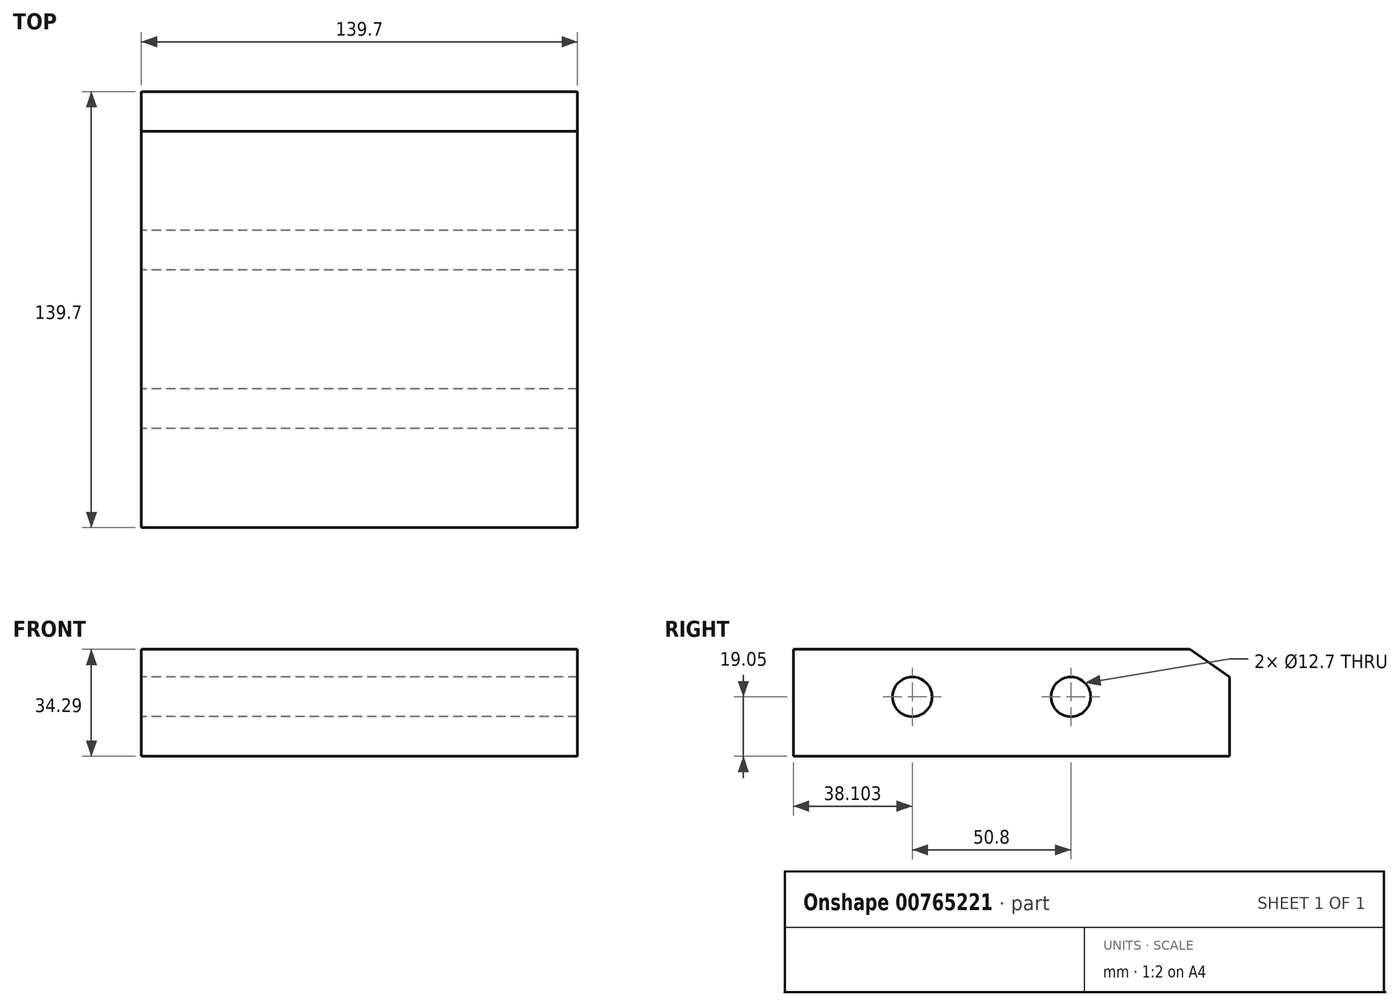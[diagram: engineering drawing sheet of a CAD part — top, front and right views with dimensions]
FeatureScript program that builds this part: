
annotation { "Feature Type Name" : "Feature", "Feature Type Description" : "" }
export const myFeature = defineFeature(function(context is Context, id is Id, definition is map)
    precondition{}
    {
        {
            var Q0;
            Q0=qCreatedBy(makeId("Right.planeOp"),FACE);
            var sketch = newSketch(context, id + "F0", { "sketchPlane" : qUnion([Q0])});
            skLineSegment(sketch, "E0", {"start": v(85.33, 0) * mm, "end": v(85.33, 15.24) * mm, "construction": true});
            skLineSegment(sketch, "E1", {"start": v(85.33, 15.24) * mm, "end": v(-41.67, 15.24) * mm});
            skLineSegment(sketch, "E2", {"start": v(-41.67, 15.24) * mm, "end": v(-41.67, -19.05) * mm});
            skLineSegment(sketch, "E3", {"start": v(-41.67, -19.05) * mm, "end": v(98.03, -19.05) * mm});
            skLineSegment(sketch, "E4", {"start": v(98.03, -19.05) * mm, "end": v(98.03, 6.35) * mm});
            skLineSegment(sketch, "E5", {"start": v(98.03, 6.35) * mm, "end": v(85.33, 15.24) * mm});
            skLineSegment(sketch, "E6", {"start": v(-41.67, 15.24) * mm, "end": v(-3.35, 15.24) * mm, "construction": true});
            skLineSegment(sketch, "E7", {"start": v(-41.67, 27.05) * mm, "end": v(-3.57, 27.05) * mm, "construction": true});
            skLineSegment(sketch, "E8", {"start": v(-41.67, 38.61) * mm, "end": v(47.23, 38.61) * mm, "construction": true});
            skCircle(sketch, "E9", {"center": v(-3.57, 0) * mm, "radius": 6.35 * mm});
            skCircle(sketch, "E10", {"center": v(47.23, 0) * mm, "radius": 6.35 * mm});
            skSolve(sketch);
        }
        {
            var Q0;
            Q0 = qSketchRegion(id + "F0", true);
            extrude(context, id + "F1", {"entities" : qUnion([Q0]), "depth" : 139.7 * mm, "offsetDistance" : 25.4 * mm});
        }
    });
